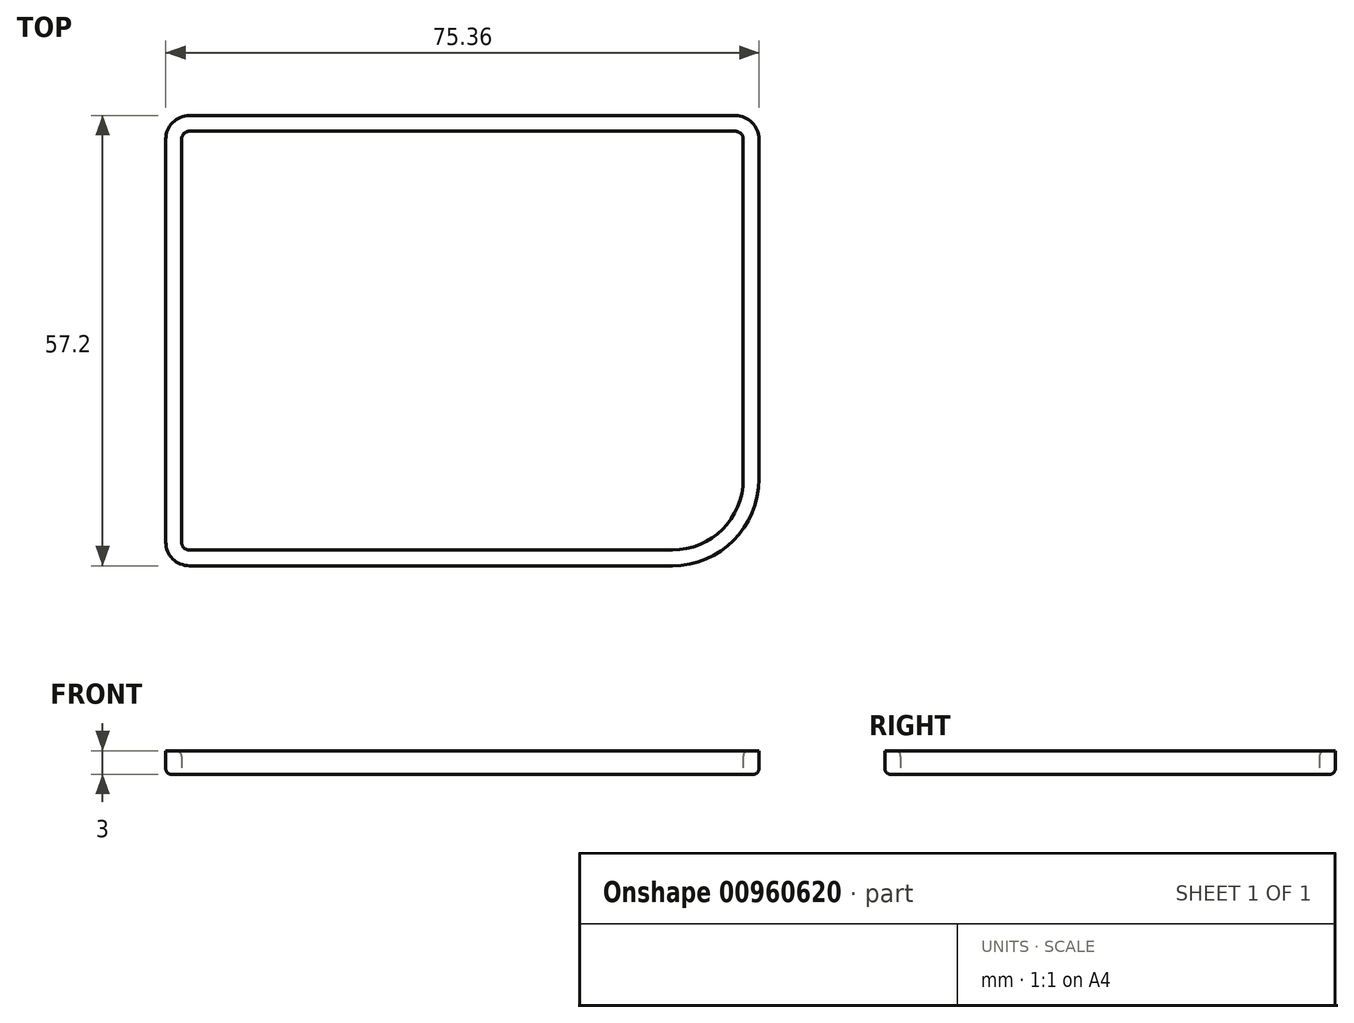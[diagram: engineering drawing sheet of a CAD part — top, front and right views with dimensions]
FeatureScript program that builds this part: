
annotation { "Feature Type Name" : "Feature", "Feature Type Description" : "" }
export const myFeature = defineFeature(function(context is Context, id is Id, definition is map)
    precondition{}
    {
        {
            var Q0;
            Q0=qCreatedBy(makeId("Top.planeOp"),FACE);
            var sketch = newSketch(context, id + "F0", { "sketchPlane" : qUnion([Q0])});
            skLineSegment(sketch, "E0.bottom", {"start": v(34.67, 28.6) * mm, "end": v(-34.67, 28.6) * mm});
            skLineSegment(sketch, "E0.top", {"start": v(26.68, -28.6) * mm, "end": v(-34.67, -28.6) * mm});
            skLineSegment(sketch, "E0.left", {"start": v(37.67, 25.6) * mm, "end": v(37.67, -17.6) * mm});
            skLineSegment(sketch, "E0.right", {"start": v(-37.67, 25.6) * mm, "end": v(-37.67, -25.6) * mm});
            skPoint(sketch, "E0.middle", {"position": v(0, 0) * mm});
            skPoint(sketch, "E1.visualSharp", {"position": v(-37.67, 28.6) * mm});
            skArc(sketch, "E1.filletArc", {"start": v(-34.67, 28.6) * mm, "mid": v(-36.8, 27.72) * mm, "end": v(-37.67, 25.6) * mm});
            skPoint(sketch, "E2.visualSharp", {"position": v(37.67, 28.6) * mm});
            skArc(sketch, "E2.filletArc", {"start": v(37.67, 25.6) * mm, "mid": v(36.8, 27.72) * mm, "end": v(34.67, 28.6) * mm});
            skPoint(sketch, "E3.visualSharp", {"position": v(-37.67, -28.6) * mm});
            skArc(sketch, "E3.filletArc", {"start": v(-37.67, -25.6) * mm, "mid": v(-36.8, -27.72) * mm, "end": v(-34.67, -28.6) * mm});
            skPoint(sketch, "E4.visualSharp", {"position": v(37.67, -28.6) * mm});
            skArc(sketch, "E4.filletArc", {"start": v(26.68, -28.6) * mm, "mid": v(34.45, -25.38) * mm, "end": v(37.67, -17.6) * mm});
            skArc(sketch, "E5.0", {"start": v(35.67, 25.6) * mm, "mid": v(35.38, 26.3) * mm, "end": v(34.67, 26.6) * mm});
            skLineSegment(sketch, "E5.1", {"start": v(35.67, 25.6) * mm, "end": v(35.67, -17.6) * mm});
            skLineSegment(sketch, "E5.2", {"start": v(34.67, 26.6) * mm, "end": v(-34.67, 26.6) * mm});
            skArc(sketch, "E5.3", {"start": v(26.68, -26.6) * mm, "mid": v(33.04, -23.96) * mm, "end": v(35.67, -17.6) * mm});
            skArc(sketch, "E5.4", {"start": v(-34.67, 26.6) * mm, "mid": v(-35.38, 26.3) * mm, "end": v(-35.67, 25.6) * mm});
            skLineSegment(sketch, "E5.5", {"start": v(-35.67, 25.6) * mm, "end": v(-35.67, -25.6) * mm});
            skArc(sketch, "E5.6", {"start": v(-35.67, -25.6) * mm, "mid": v(-35.38, -26.3) * mm, "end": v(-34.67, -26.6) * mm});
            skLineSegment(sketch, "E5.7", {"start": v(26.68, -26.6) * mm, "end": v(-34.67, -26.6) * mm});
            skSolve(sketch);
        }
        {
            var Q0;
            Q0=makeQuery(id+"F0.imprint","IMPRINT",FACE,{"disambiguationData":[TD([[makeQuery(id+"F0.imprint","IMPRINT",EDGE,{"derivedFrom":sQuery(id+"F0.wireOp",EDGE,"E0.bottom")}),1.0]])]});
            extrude(context, id + "F1", {"entities" : qUnion([Q0]), "depth" : 3 * mm, "offsetDistance" : 25 * mm});
        }
        {
            var Q0;
            Q0=makeQuery(id+"F1.opExtrude","CAP_EDGE",EDGE,{"disambiguationData":[OSD([sQuery(id+"F0.wireOp",EDGE,"E0.right")])],"isStart":true});
            var Q1;
            Q1=makeQuery(id+"F1.opExtrude","CAP_EDGE",EDGE,{"disambiguationData":[OSD([sQuery(id+"F0.wireOp",EDGE,"E5.2")])],"isStart":false});
            var Q2;
            Q2=makeQuery(id+"F1.opExtrude","CAP_EDGE",EDGE,{"disambiguationData":[OSD([sQuery(id+"F0.wireOp",EDGE,"E5.5")])],"isStart":false});
            var Q3;
            Q3=makeQuery(id+"F1.opExtrude","CAP_EDGE",EDGE,{"disambiguationData":[OSD([sQuery(id+"F0.wireOp",EDGE,"E5.1")])],"isStart":false});
            fillet(context, id + "F2", {"entities" : qUnion([Q0, Q1, Q2, Q3]), "radius" : .7 * mm, "tangentPropagation" : true, "allowEdgeOverflow" : false});
        }
    });
